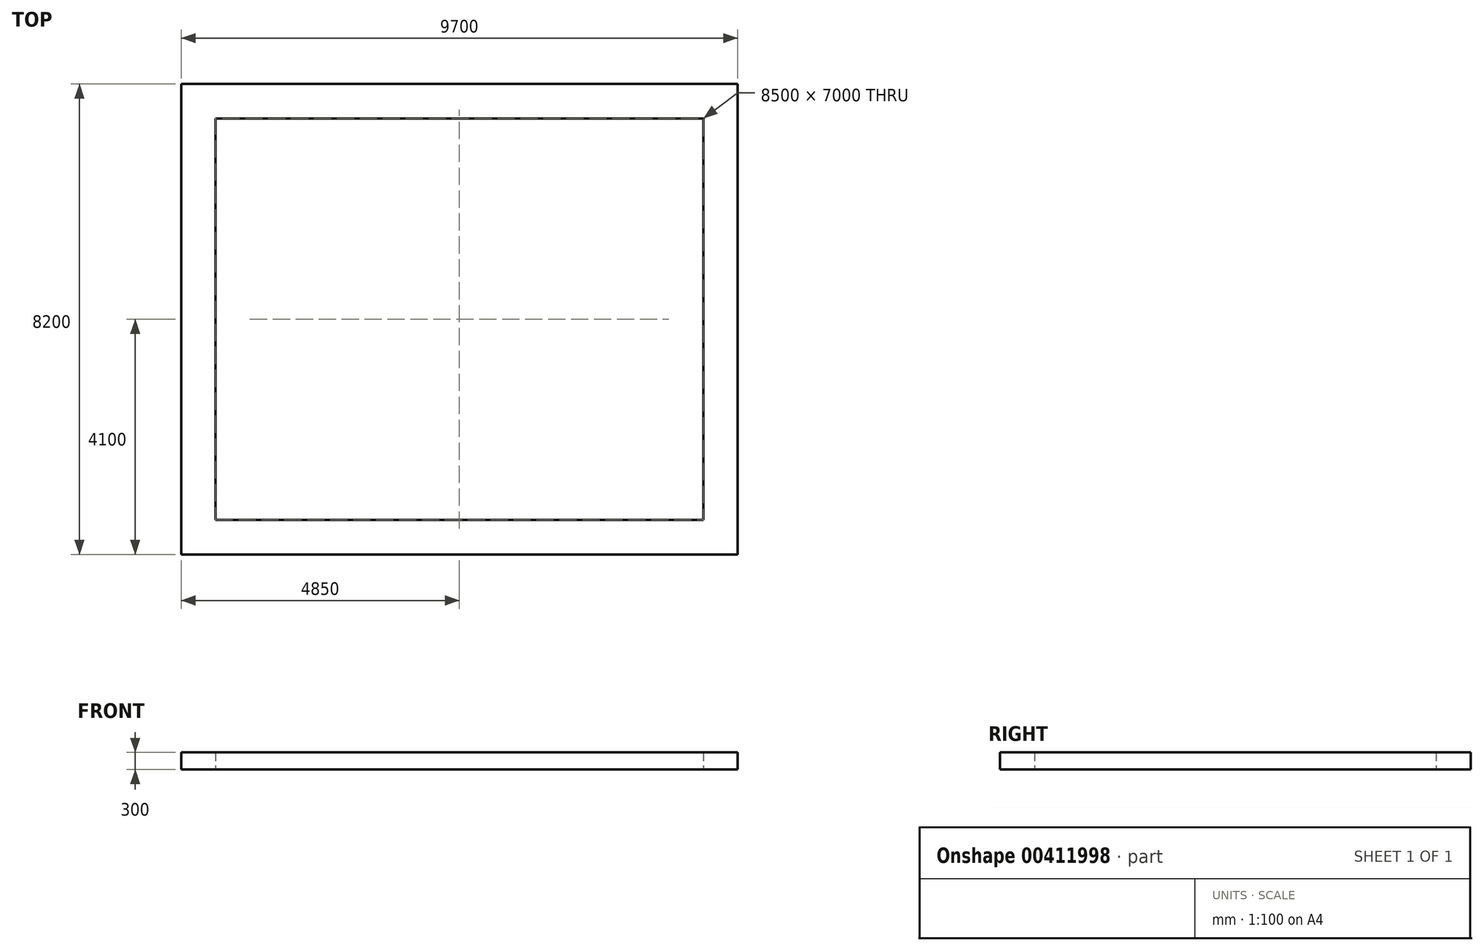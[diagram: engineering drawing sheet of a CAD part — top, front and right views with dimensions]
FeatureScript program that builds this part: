
annotation { "Feature Type Name" : "Feature", "Feature Type Description" : "" }
export const myFeature = defineFeature(function(context is Context, id is Id, definition is map)
    precondition{}
    {
        {
            var Q0;
            Q0=qCreatedBy(makeId("Top.planeOp"),FACE);
            var sketch = newSketch(context, id + "F0", { "sketchPlane" : qUnion([Q0])});
            skLineSegment(sketch, "E0.bottom", {"start": v(0, 0) * mm, "end": v(8500, 0) * mm});
            skLineSegment(sketch, "E0.top", {"start": v(0, 7000) * mm, "end": v(8500, 7000) * mm});
            skLineSegment(sketch, "E0.left", {"start": v(0, 0) * mm, "end": v(0, 7000) * mm});
            skLineSegment(sketch, "E0.right", {"start": v(8500, 0) * mm, "end": v(8500, 7000) * mm});
            skSolve(sketch);
        }
        {
            var Q0;
            Q0 = qSketchRegion(id + "F0", true);
            extrude(context, id + "F1", {"entities" : qUnion([Q0]), "depth" : 300 * mm});
        }
        {
            var Q0;
            Q0=qCreatedBy(makeId("Top.planeOp"),FACE);
            var sketch = newSketch(context, id + "F2", { "sketchPlane" : qUnion([Q0])});
            skLineSegment(sketch, "E1.bottom", {"start": v(0, 7000) * mm, "end": v(8500, 7000) * mm});
            skLineSegment(sketch, "E1.top", {"start": v(0, 0) * mm, "end": v(8500, 0) * mm});
            skLineSegment(sketch, "E1.left", {"start": v(0, 7000) * mm, "end": v(0, 0) * mm});
            skLineSegment(sketch, "E1.right", {"start": v(8500, 7000) * mm, "end": v(8500, 0) * mm});
            skLineSegment(sketch, "E2.bottom", {"start": v(-600, 7600) * mm, "end": v(9100, 7600) * mm});
            skLineSegment(sketch, "E2.top", {"start": v(-600, -600) * mm, "end": v(9100, -600) * mm});
            skLineSegment(sketch, "E2.left", {"start": v(-600, 7600) * mm, "end": v(-600, -600) * mm});
            skLineSegment(sketch, "E2.right", {"start": v(9100, 7600) * mm, "end": v(9100, -600) * mm});
            skSolve(sketch);
        }
        {
            var Q0;
            Q0 = qSketchRegion(id + "F2", true);
            var Q1;
            Q1=makeQuery(id+"F1.opExtrude","CAP_FACE",FACE,{"disambiguationData":[OSD([sQuery(id+"F0.wireOp",EDGE,"E0.bottom"),sQuery(id+"F0.wireOp",EDGE,"E0.top"),sQuery(id+"F0.wireOp",EDGE,"E0.left"),sQuery(id+"F0.wireOp",EDGE,"E0.right")])],"isStart":false});
            extrude(context, id + "F3", {"entities" : qUnion([Q0]), "endBound" : BoundingType.UP_TO_SURFACE, "endBoundEntityFace" : qUnion([Q1]), "depth" : 25 * mm});
        }
    });
